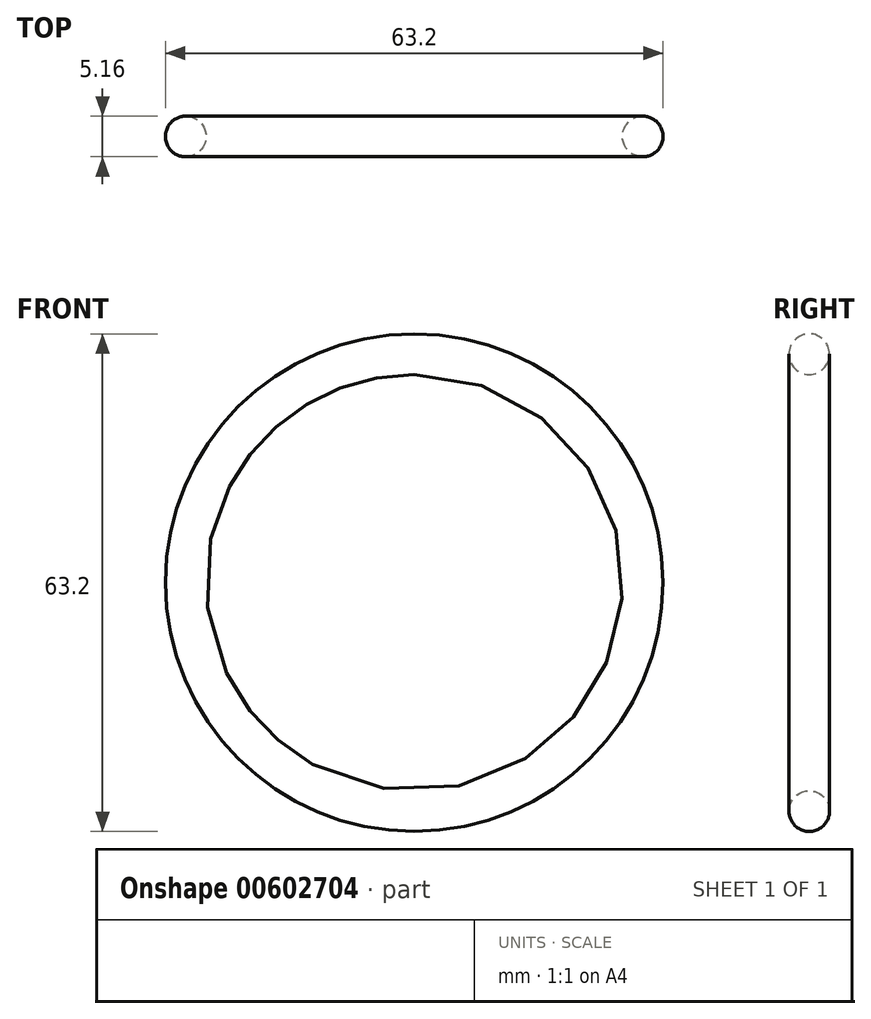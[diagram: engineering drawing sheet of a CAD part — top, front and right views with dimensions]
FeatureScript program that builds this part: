
annotation { "Feature Type Name" : "Feature", "Feature Type Description" : "" }
export const myFeature = defineFeature(function(context is Context, id is Id, definition is map)
    precondition{}
    {
        {
            var Q0;
            Q0=qCreatedBy(makeId("Front.planeOp"),FACE);
            var sketch = newSketch(context, id + "F0", { "sketchPlane" : qUnion([Q0])});
            skCircle(sketch, "E0", {"center": v(0, 0) * mm, "radius": 19.05 * mm});
            skSolve(sketch);
        }
        {
            var Q0;
            Q0=qCreatedBy(makeId("Right.planeOp"),FACE);
            var sketch = newSketch(context, id + "F1", { "sketchPlane" : qUnion([Q0])});
            skCircle(sketch, "E1", {"center": v(0, 29.02) * mm, "radius": 2.58 * mm});
            skSolve(sketch);
        }
        {
            var Q0;
            Q0=makeQuery(id+"F1.imprint","IMPRINT",FACE,{"disambiguationData":[TD([[makeQuery(id+"F1.imprint","IMPRINT",EDGE,{"derivedFrom":sQuery(id+"F1.wireOp",EDGE,"E1")}),1.0]])]});
            var Q1;
            Q1=sQuery(id+"F0.wireOp",EDGE,"E0");
            revolve(context, id + "F2", {"entities" : qUnion([Q0]), "axis" : qUnion([Q1]), "revolveType" : RevolveType.FULL});
        }
    });
